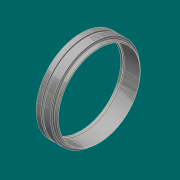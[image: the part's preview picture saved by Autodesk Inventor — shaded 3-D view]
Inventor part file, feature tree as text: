
AUTODESK INVENTOR PART (.ipt)
format: ipt  version: 2017.3 (Build 213256000, 256)  size: 226,816 bytes
history: native  units: in
note: dims shown in document units (in); Inventor stores cm internally (conversion verified against a paired STEP export)
features: revolve x1, chamfer x1, sketch x1
ambient origin geometry x8: Origin, YZ Plane, XZ Plane, XY Plane, X Axis, Y Axis, Z Axis, Center Point
bodies: Solid1 (feature_tree)
feature tree (3):
  revolve  "Revolution1"  [1 undecoded]
  chamfer  "Chamfer2"  Distance=18.0in
  sketch  "Sketch1"  dims[d0=19.25in d1=6.1875in d3=18.0in d5=0.3125in d10=0.25in d12=17.25in d13=2.05in d16=90.0deg d17=0.375in d29=0.0312in d30=0.125in d31=45.0deg d32=0.5in d35=1.0in d38=0.0687in d39=0.1374in d40=0.895in d41=0.6in d44=8.0in d45=0.2577in d47=0.375in]
note: 1 required parameter value undecoded (feature->parameter linkage not recoverable at this tier; creation-order binding heuristic only, values carry confidence <= 0.55)
